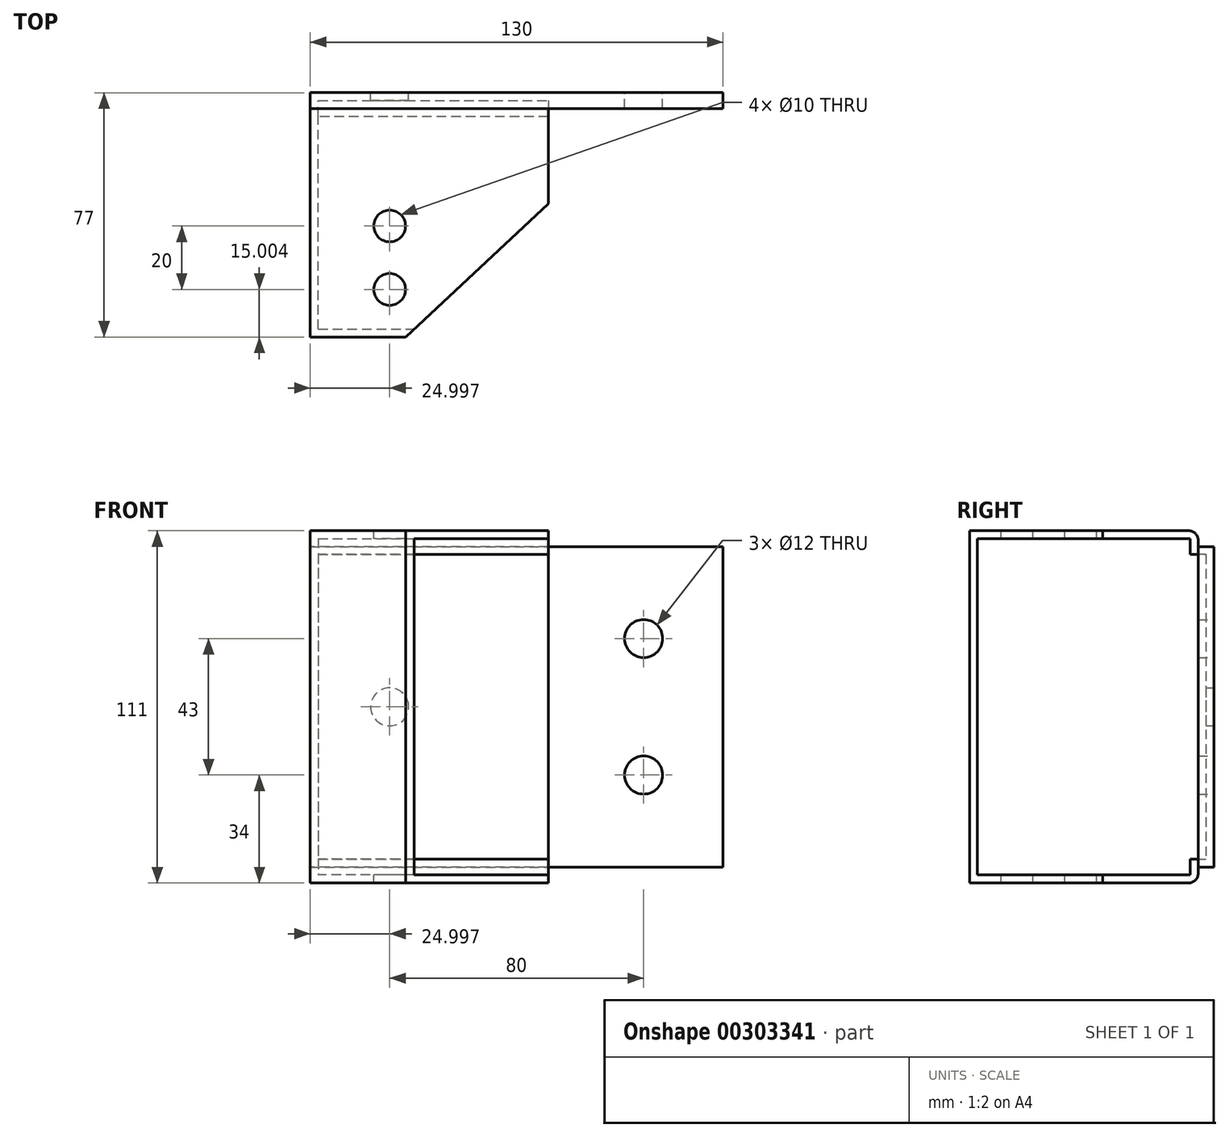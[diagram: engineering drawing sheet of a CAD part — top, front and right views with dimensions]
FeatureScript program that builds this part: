
annotation { "Feature Type Name" : "Feature", "Feature Type Description" : "" }
export const myFeature = defineFeature(function(context is Context, id is Id, definition is map)
    precondition{}
    {
        {
            var Q0;
            Q0=qCreatedBy(makeId("Top.planeOp"),FACE);
            var sketch = newSketch(context, id + "F0", { "sketchPlane" : qUnion([Q0])});
            skLineSegment(sketch, "E0", {"start": v(-59.95, -25.66) * mm, "end": v(-59.95, 51.34) * mm});
            skLineSegment(sketch, "E1", {"start": v(-59.95, 51.34) * mm, "end": v(70.05, 51.34) * mm});
            skLineSegment(sketch, "E2", {"start": v(70.05, 51.34) * mm, "end": v(70.05, 46.34) * mm});
            skLineSegment(sketch, "E3", {"start": v(70.05, 46.34) * mm, "end": v(15.05, 46.34) * mm});
            skLineSegment(sketch, "E4", {"start": v(15.05, 46.34) * mm, "end": v(15.05, 16.34) * mm});
            skLineSegment(sketch, "E5", {"start": v(-59.95, -25.66) * mm, "end": v(-29.95, -25.66) * mm});
            skLineSegment(sketch, "E6", {"start": v(-29.95, -25.66) * mm, "end": v(15.05, 16.34) * mm});
            skLineSegment(sketch, "E7", {"start": v(15.05, 46.34) * mm, "end": v(-59.95, 46.34) * mm});
            skSolve(sketch);
        }
        {
            var Q0;
            Q0=makeQuery(id+"F0.imprint","IMPRINT",FACE,{"disambiguationData":[TD([[makeQuery(id+"F0.imprint","IMPRINT",EDGE,{"derivedFrom":sQuery(id+"F0.wireOp",EDGE,"E4")}),-1.0]])]});
            extrude(context, id + "F1", {"entities" : qUnion([Q0]), "depth" : 55.5 * mm, "hasSecondDirection" : true, "secondDirectionOppositeDirection" : true, "secondDirectionDepth" : 55.5 * mm});
        }
        {
            var Q0;
            Q0 = qSketchRegion(id + "F0", true);
            extrude(context, id + "F2", {"entities" : qUnion([Q0]), "operationType" : NewBodyOperationType.ADD, "depth" : 50.5 * mm, "hasSecondDirection" : true, "secondDirectionOppositeDirection" : true, "secondDirectionDepth" : 50.5 * mm});
        }
        {
            var Q0;
            Q0=makeQuery(id+"F2.opExtrude","SWEPT_FACE",FACE,{"disambiguationData":[OSD([sQuery(id+"F0.wireOp",EDGE,"E1")])]});
            var sketch = newSketch(context, id + "F3", { "sketchPlane" : qUnion([Q0])});
            skCircle(sketch, "E8", {"center": v(-45.05, -21.5) * mm, "radius": 6 * mm});
            skCircle(sketch, "E9", {"center": v(-45.05, 21.5) * mm, "radius": 6 * mm});
            skPoint(sketch, "E10.endSnap0", {"position": v(59.95, 0) * mm});
            skCircle(sketch, "E11", {"center": v(34.95, 0) * mm, "radius": 6 * mm});
            skPoint(sketch, "E10.start.orphan", {"position": v(59.95, 0) * mm});
            skSolve(sketch);
        }
        {
            var Q0;
            Q0=makeQuery(id+"F3.imprint","IMPRINT",FACE,{"disambiguationData":[TD([[makeQuery(id+"F3.imprint","IMPRINT",EDGE,{"derivedFrom":sQuery(id+"F3.wireOp",EDGE,"E8")}),1.0]])]});
            var Q1;
            Q1=makeQuery(id+"F3.imprint","IMPRINT",FACE,{"disambiguationData":[TD([[makeQuery(id+"F3.imprint","IMPRINT",EDGE,{"derivedFrom":sQuery(id+"F3.wireOp",EDGE,"E9")}),1.0]])]});
            extrude(context, id + "F4", {"entities" : qUnion([Q0, Q1]), "operationType" : NewBodyOperationType.REMOVE, "oppositeDirection" : true, "depth" : 25 * mm});
        }
        {
            var Q0;
            Q0=makeQuery(id+"F1.opExtrude","SWEPT_FACE",FACE,{"disambiguationData":[OSD([sQuery(id+"F0.wireOp",EDGE,"E4")])]});
            var Q1;
            Q1=makeQuery(id+"F1.opExtrude","SWEPT_FACE",FACE,{"disambiguationData":[OSD([sQuery(id+"F0.wireOp",EDGE,"E6")])]});
            shell(context, id + "F5", {"entities" : qUnion([Q0, Q1]), "thickness" : 2.5 * mm});
        }
        {
            var Q0;
            Q0=makeQuery(id+"F1.opExtrude","CAP_FACE",FACE,{"disambiguationData":[OSD([sQuery(id+"F0.wireOp",EDGE,"E0"),sQuery(id+"F0.wireOp",EDGE,"E4"),sQuery(id+"F0.wireOp",EDGE,"E5"),sQuery(id+"F0.wireOp",EDGE,"E6"),sQuery(id+"F0.wireOp",EDGE,"E7")])],"isStart":false});
            var sketch = newSketch(context, id + "F6", { "sketchPlane" : qUnion([Q0])});
            skCircle(sketch, "E12", {"center": v(-34.95, 9.34) * mm, "radius": 5 * mm});
            skCircle(sketch, "E13", {"center": v(-34.95, -10.66) * mm, "radius": 5 * mm});
            skSolve(sketch);
        }
        {
            var Q0;
            Q0=makeQuery(id+"F6.imprint","IMPRINT",FACE,{"disambiguationData":[TD([[makeQuery(id+"F6.imprint","IMPRINT",EDGE,{"derivedFrom":sQuery(id+"F6.wireOp",EDGE,"E12")}),1.0]])]});
            var Q1;
            Q1=makeQuery(id+"F6.imprint","IMPRINT",FACE,{"disambiguationData":[TD([[makeQuery(id+"F6.imprint","IMPRINT",EDGE,{"derivedFrom":sQuery(id+"F6.wireOp",EDGE,"E13")}),1.0]])]});
            extrude(context, id + "F7", {"entities" : qUnion([Q0, Q1]), "operationType" : NewBodyOperationType.REMOVE, "oppositeDirection" : true, "depth" : 157.2 * mm});
        }
        {
            var Q0;
            Q0 = qSketchRegion(id + "F3", true);
            extrude(context, id + "F8", {"entities" : qUnion([Q0]), "operationType" : NewBodyOperationType.REMOVE, "oppositeDirection" : true, "depth" : 25 * mm});
        }
        {
            var Q0;
            Q0=makeQuery(id+"F1.opExtrude","CAP_EDGE",EDGE,{"disambiguationData":[OSD([sQuery(id+"F0.wireOp",EDGE,"E7")])],"isStart":true});
            var Q1;
            Q1=makeQuery(id+"F1.opExtrude","CAP_EDGE",EDGE,{"disambiguationData":[OSD([sQuery(id+"F0.wireOp",EDGE,"E7")])],"isStart":false});
            fillet(context, id + "F9", {"entities" : qUnion([Q0, Q1]), "radius" : 3 * mm, "tangentPropagation" : true, "allowEdgeOverflow" : false});
        }
    });
